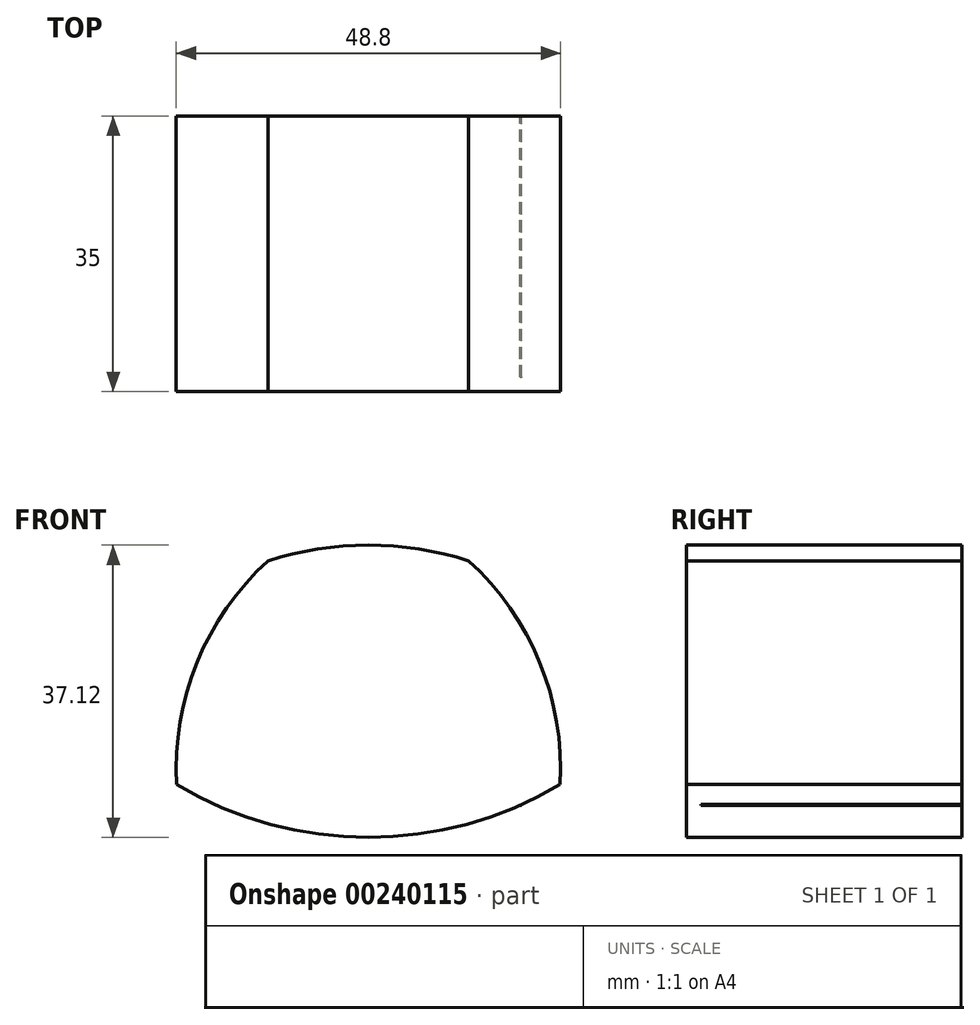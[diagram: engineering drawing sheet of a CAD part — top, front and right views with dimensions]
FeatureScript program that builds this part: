
annotation { "Feature Type Name" : "Feature", "Feature Type Description" : "" }
export const myFeature = defineFeature(function(context is Context, id is Id, definition is map)
    precondition{}
    {
        {
            var Q0;
            Q0=qCreatedBy(makeId("Front.planeOp"),FACE);
            var sketch = newSketch(context, id + "F0", { "sketchPlane" : qUnion([Q0])});
            skArc(sketch, "E0", {"start": v(-12.74, 17.25) * mm, "mid": v(-21.76, 4.35) * mm, "end": v(-24.34, -11.2) * mm});
            skArc(sketch, "E1", {"start": v(12.74, 17.25) * mm, "mid": v(0, 19.23) * mm, "end": v(-12.74, 17.25) * mm});
            skLineSegment(sketch, "E2", {"start": v(0, 44.76) * mm, "end": v(0, -42.14) * mm, "construction": true});
            skArc(sketch, "E3.MirrorCS", {"start": v(12.74, 17.25) * mm, "mid": v(21.76, 4.35) * mm, "end": v(24.34, -11.2) * mm});
            skArc(sketch, "E4", {"start": v(-24.34, -11.2) * mm, "mid": v(0, -17.89) * mm, "end": v(24.34, -11.2) * mm});
            skSolve(sketch);
        }
        {
            var Q0;
            Q0=makeQuery(id+"F0.imprint","IMPRINT",FACE,{"disambiguationData":[TD([[makeQuery(id+"F0.imprint","IMPRINT",EDGE,{"derivedFrom":sQuery(id+"F0.wireOp",EDGE,"E0")}),1.0]])]});
            extrude(context, id + "F1", {"entities" : qUnion([Q0]), "depth" : 10 * mm});
        }
        {
            var Q0;
            Q0=makeQuery(id+"F1.opExtrude","CAP_FACE",FACE,{"disambiguationData":[OSD([sQuery(id+"F0.wireOp",EDGE,"E0"),sQuery(id+"F0.wireOp",EDGE,"E1"),sQuery(id+"F0.wireOp",EDGE,"E3.MirrorCS"),sQuery(id+"F0.wireOp",EDGE,"E4")])],"isStart":false});
            var sketch = newSketch(context, id + "F2", { "sketchPlane" : qUnion([Q0])});
            skLineSegment(sketch, "E5", {"start": v(-23.7, -2.11) * mm, "end": v(23.7, -2.11) * mm});
            skSolve(sketch);
        }
        {
            var Q0;
            Q0=qCreatedBy(makeId("Right.planeOp"),FACE);
            var sketch = newSketch(context, id + "F3", { "sketchPlane" : qUnion([Q0])});
            skArc(sketch, "E6", {"start": v(-11.15, -2.6) * mm, "mid": v(-8.03, -14) * mm, "end": v(0, -22.66) * mm});
            skSolve(sketch);
        }
        {
            var Q0;
            Q0=qCreatedBy(makeId("Right.planeOp"),FACE);
            cPlane(context, id + "F4", {"entities" : qUnion([Q0]), "cplaneType" : CPlaneType.OFFSET, "offset" : 25 * mm, "width" : 150 * mm, "height" : 150 * mm});
        }
        {
            var Q0;
            Q0=qCreatedBy(id+"F4.planeOp",FACE);
            var sketch = newSketch(context, id + "F5", { "sketchPlane" : qUnion([Q0])});
            skPoint(sketch, "E7.0", {"position": v(-10, -2.11) * mm});
            skPoint(sketch, "E8.0", {"position": v(0, -11.2) * mm});
            skArc(sketch, "E9", {"start": v(-10, -2.11) * mm, "mid": v(-6.4, -8.2) * mm, "end": v(0, -11.2) * mm});
            skSolve(sketch);
        }
        {
            var Q0;
            {var subQ0=sQuery(id+"F2.wireOp",EDGE,"E5");Q0=makeQuery(id+"F2.imprint","IMPRINT",FACE,{"disambiguationData":[TD([[makeQuery(id+"F2.imprint","IMPRINT",EDGE,{"derivedFrom":subQ0}),-1.0]])]});}
            var sketch = newSketch(context, id + "F6", { "sketchPlane" : qUnion([Q0])});
            skPoint(sketch, "E10.0", {"position": v(0, -2.11) * mm});
            skLineSegment(sketch, "E11", {"start": v(0, -2.11) * mm, "end": v(40.09, -2.11) * mm});
            skLineSegment(sketch, "E12", {"start": v(40.09, -2.11) * mm, "end": v(40.8, -19.06) * mm});
            skLineSegment(sketch, "E13", {"start": v(40.8, -19.06) * mm, "end": v(0, -22.55) * mm});
            skLineSegment(sketch, "E14", {"start": v(0, -22.55) * mm, "end": v(0, -2.11) * mm});
            skSolve(sketch);
        }
        {
            var Q0;
            {var subQ5=sQuery(id+"F6.wireOp",EDGE,"E12");Q0=makeQuery(id+"F6.imprint","IMPRINT",FACE,{"disambiguationData":[TD([[makeQuery(id+"F6.imprint","IMPRINT",EDGE,{"derivedFrom":subQ5}),-1.0]])]});}
            var Q1;
            {var subQ1=makeQuery(id+"F1.opExtrude","CAP_EDGE",EDGE,{"disambiguationData":[OSD([sQuery(id+"F0.wireOp",EDGE,"E4")])],"isStart":false});var subQ2=makeQuery(id+"F1.opExtrude","CAP_EDGE",EDGE,{"disambiguationData":[OSD([sQuery(id+"F0.wireOp",EDGE,"E3.MirrorCS")])],"isStart":false});var subQ4=makeQuery(id+"F2.imprint","IMPRINT",EDGE,{"disambiguationData":[TD([[makeQuery(id+"F2.imprint","INTERSECT",VERTEX,{"derivedFrom":[subQ2,subQ1]}),1.0]])],"derivedFrom":subQ2});Q1=makeQuery(id+"F6.imprint","IMPRINT",FACE,{"disambiguationData":[TD([[makeQuery(id+"F6.imprint","IMPRINT",EDGE,{"derivedFrom":subQ4}),-1.0]])]});}
            var Q2;
            Q2=makeQuery(id+"FwF9H4vXaNREEru_1.opLoft","SWEPT_FACE",FACE,{"disambiguationData":[OSD([sQuery(id+"F3.wireOp",VERTEX,"E6.start"),sQuery(id+"F3.wireOp",VERTEX,"E6.end"),sQuery(id+"F3.wireOp",EDGE,"E6"),sQuery(id+"F5.wireOp",VERTEX,"E9.start"),sQuery(id+"F5.wireOp",VERTEX,"E9.end"),sQuery(id+"F5.wireOp",EDGE,"E9")])]});
            extrude(context, id + "F7", {"entities" : qUnion([Q0, Q1]), "operationType" : NewBodyOperationType.REMOVE, "endBound" : BoundingType.THROUGH_ALL, "oppositeDirection" : true, "endBoundEntityFace" : qUnion([Q2]), "depth" : 25 * mm});
        }
        {
            var Q0;
            Q0=makeQuery(id+"F1.opExtrude","CAP_FACE",FACE,{"disambiguationData":[OSD([sQuery(id+"F0.wireOp",EDGE,"E0"),sQuery(id+"F0.wireOp",EDGE,"E1"),sQuery(id+"F0.wireOp",EDGE,"E3.MirrorCS"),sQuery(id+"F0.wireOp",EDGE,"E4")])],"isStart":true});
            extrude(context, id + "F8", {"entities" : qUnion([Q0]), "operationType" : NewBodyOperationType.ADD, "depth" : 25 * mm});
        }
        {
            var Q0;
            Q0=makeQuery(id+"F8.opExtrude","CAP_FACE",FACE,{"disambiguationData":[OSD([sQuery(id+"F0.wireOp",EDGE,"E0"),sQuery(id+"F0.wireOp",EDGE,"E1"),sQuery(id+"F0.wireOp",EDGE,"E3.MirrorCS"),sQuery(id+"F0.wireOp",EDGE,"E4")])],"isStart":false});
            var sketch = newSketch(context, id + "F9", { "sketchPlane" : qUnion([Q0])});
            skLineSegment(sketch, "E15.bottom", {"start": v(0, -2.11) * mm, "end": v(-23.7, -2.11) * mm});
            skLineSegment(sketch, "E15.top", {"start": v(0, -17.89) * mm, "end": v(-23.7, -17.89) * mm});
            skLineSegment(sketch, "E15.left", {"start": v(0, -2.11) * mm, "end": v(0, -17.89) * mm});
            skLineSegment(sketch, "E15.right", {"start": v(-23.7, -2.11) * mm, "end": v(-23.7, -17.89) * mm});
            skLineSegment(sketch, "E16.bottom", {"start": v(-3.23, -13.8) * mm, "end": v(-19.48, -13.8) * mm});
            skLineSegment(sketch, "E16.top", {"start": v(-3.23, -5.57) * mm, "end": v(-19.48, -5.57) * mm});
            skLineSegment(sketch, "E16.left", {"start": v(-3.23, -13.8) * mm, "end": v(-3.23, -5.57) * mm});
            skLineSegment(sketch, "E16.right", {"start": v(-19.48, -13.8) * mm, "end": v(-19.48, -5.57) * mm});
            skSolve(sketch);
        }
        {
            var Q0;
            Q0=sQuery(id+"F3.wireOp",EDGE,"E6");
            extrude(context, id + "F10", {"bodyType" : ToolBodyType.SURFACE, "surfaceEntities" : qUnion([Q0]), "depth" : 25 * mm});
        }
        {
            var Q0;
            Q0=makeQuery(id+"F9.imprint","IMPRINT",FACE,{"disambiguationData":[TD([[makeQuery(id+"F9.imprint","IMPRINT",EDGE,{"derivedFrom":sQuery(id+"F9.wireOp",EDGE,"E16.bottom")}),-1.0]])]});
            var Q1;
            Q1=makeQuery(id+"F10.opExtrude","SWEPT_FACE",FACE,{"disambiguationData":[OSD([sQuery(id+"F3.wireOp",EDGE,"E6")])]});
            extrude(context, id + "F11", {"entities" : qUnion([Q0]), "endBound" : BoundingType.UP_TO_SURFACE, "oppositeDirection" : true, "endBoundEntityFace" : qUnion([Q1]), "depth" : 25 * mm});
        }
    });
